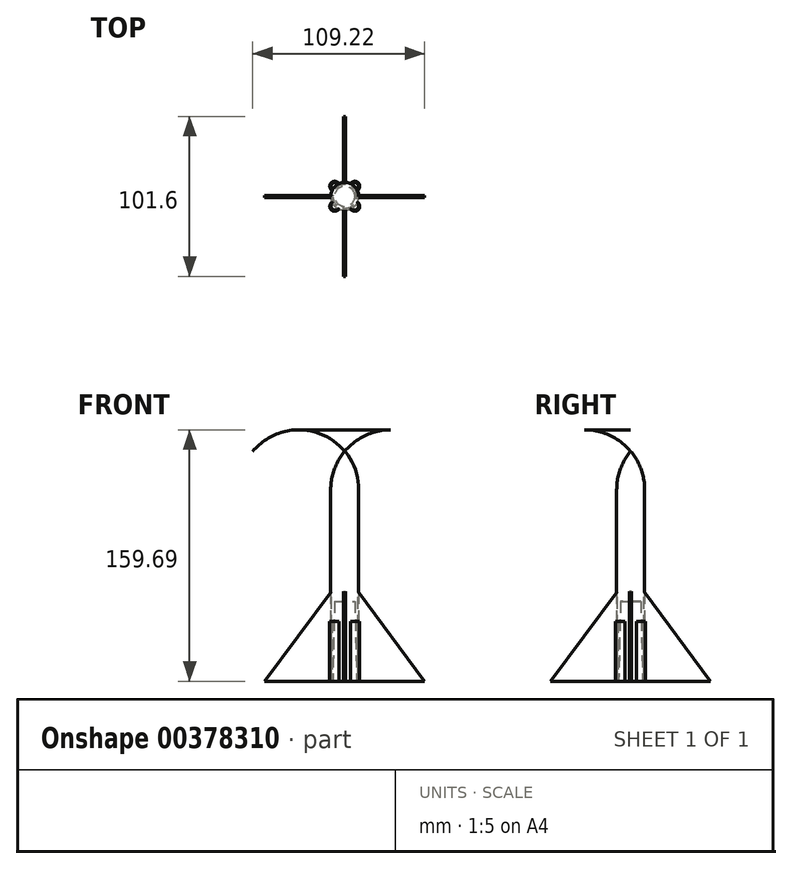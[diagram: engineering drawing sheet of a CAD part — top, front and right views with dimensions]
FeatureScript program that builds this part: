
annotation { "Feature Type Name" : "Feature", "Feature Type Description" : "" }
export const myFeature = defineFeature(function(context is Context, id is Id, definition is map)
    precondition{}
    {
        {
            var Q0;
            Q0=qCreatedBy(makeId("Front.planeOp"),FACE);
            var sketch = newSketch(context, id + "F0", { "sketchPlane" : qUnion([Q0])});
            skLineSegment(sketch, "E0", {"start": v(8.89, 0) * mm, "end": v(8.89, 121.59) * mm});
            skArc(sketch, "E1", {"start": v(8.89, 121.59) * mm, "mid": v(6.6, 134.6) * mm, "end": v(0, 146.05) * mm});
            skLineSegment(sketch, "E2", {"start": v(8.89, 0) * mm, "end": v(7.62, 0) * mm});
            skLineSegment(sketch, "E3", {"start": v(0, 146.05) * mm, "end": v(0, 50.8) * mm});
            skLineSegment(sketch, "E4", {"start": v(0, 50.8) * mm, "end": v(6.48, 50.8) * mm});
            skLineSegment(sketch, "E5", {"start": v(6.48, 50.8) * mm, "end": v(7.62, 0) * mm});
            skSolve(sketch);
        }
        {
            var Q0;
            Q0=qCreatedBy(makeId("Front.planeOp"),FACE);
            var sketch = newSketch(context, id + "F1", { "sketchPlane" : qUnion([Q0])});
            skLineSegment(sketch, "E6", {"start": v(0, 0) * mm, "end": v(0, 146.05) * mm, "construction": true});
            skSolve(sketch);
        }
        {
            var Q0;
            Q0 = qSketchRegion(id + "F0", true);
            var Q1;
            Q1=sQuery(id+"F1.wireOp",EDGE,"E6");
            revolve(context, id + "F2", {"entities" : qUnion([Q0]), "axis" : qUnion([Q1]), "revolveType" : RevolveType.FULL});
        }
        {
            var Q0;
            Q0=qCreatedBy(makeId("Front.planeOp"),FACE);
            var sketch = newSketch(context, id + "F3", { "sketchPlane" : qUnion([Q0])});
            skLineSegment(sketch, "E7", {"start": v(8.38, 0) * mm, "end": v(8.38, 57.15) * mm});
            skLineSegment(sketch, "E8", {"start": v(50.8, 0) * mm, "end": v(8.38, 0) * mm});
            skLineSegment(sketch, "E9", {"start": v(50.8, 0) * mm, "end": v(8.38, 57.15) * mm});
            skSolve(sketch);
        }
        {
            var Q0;
            Q0=makeQuery(id+"F3.imprint","IMPRINT",FACE,{"disambiguationData":[TD([[makeQuery(id+"F3.imprint","IMPRINT",EDGE,{"derivedFrom":sQuery(id+"F3.wireOp",EDGE,"E7")}),-1.0]])]});
            extrude(context, id + "F4", {"entities" : qUnion([Q0]), "endBound" : BoundingType.SYMMETRIC, "oppositeDirection" : true, "depth" : 1.27 * mm});
        }
        {
            var Q0;
            Q0=makeQuery(id+"F4.opExtrude","SWEPT_BODY",BODY,{"disambiguationData":[OSD([sQuery(id+"F3.wireOp",EDGE,"E7"),sQuery(id+"F3.wireOp",EDGE,"E8"),sQuery(id+"F3.wireOp",EDGE,"AmAJtCWf-JhnC-Zdbh-OpwC-5Ge9B8AHfaNN"),sQuery(id+"F3.wireOp",EDGE,"CZrF4tDa-VywW-QGTz-fQES-1TtyQ9VBaDYf"),sQuery(id+"F3.wireOp",EDGE,"y0zfwKda-kGy6-blsG-hRF5-Mtb7aMOzeKxd"),sQuery(id+"F3.wireOp",EDGE,"E9")])]});
            var Q1;
            Q1=makeQuery(id+"F2.opRevolve","SWEPT_FACE",FACE,{"disambiguationData":[OSD([sQuery(id+"F0.wireOp",EDGE,"E0")])]});
            circularPattern(context, id + "F5", {"entities" : qUnion([Q0]), "axis" : qUnion([Q1]), "angle" : 360 * degree, "instanceCount" : 4, "oppositeDirection" : true, "equalSpace" : true});
        }
        {
            var Q0;
            Q0=qCreatedBy(makeId("Top.planeOp"),FACE);
            var sketch = newSketch(context, id + "F6", { "sketchPlane" : qUnion([Q0])});
            skPoint(sketch, "E10.center", {"position": v(0, 0) * mm});
            skArc(sketch, "E11", {"start": v(-8.09, 3.7) * mm, "mid": v(-8.6, 8.6) * mm, "end": v(-3.7, 8.09) * mm});
            skArc(sketch, "E12.1.0", {"start": v(-3.7, -8.09) * mm, "mid": v(-8.6, -8.6) * mm, "end": v(-8.09, -3.7) * mm});
            skArc(sketch, "E12.2.0", {"start": v(8.09, -3.7) * mm, "mid": v(8.6, -8.6) * mm, "end": v(3.7, -8.09) * mm});
            skArc(sketch, "E12.3.0", {"start": v(3.7, 8.09) * mm, "mid": v(8.6, 8.6) * mm, "end": v(8.09, 3.7) * mm});
            skArc(sketch, "E13", {"start": v(-7.98, -3.92) * mm, "mid": v(-7.98, -7.98) * mm, "end": v(-3.92, -7.98) * mm});
            skArc(sketch, "E14.1.0", {"start": v(3.92, -7.98) * mm, "mid": v(7.98, -7.98) * mm, "end": v(7.98, -3.92) * mm});
            skArc(sketch, "E14.2.0", {"start": v(7.98, 3.92) * mm, "mid": v(7.98, 7.98) * mm, "end": v(3.92, 7.98) * mm});
            skArc(sketch, "E14.3.0", {"start": v(-3.92, 7.98) * mm, "mid": v(-7.98, 7.98) * mm, "end": v(-7.98, 3.92) * mm});
            skLineSegment(sketch, "E15", {"start": v(-8.09, -3.7) * mm, "end": v(-7.98, -3.92) * mm});
            skLineSegment(sketch, "E16", {"start": v(-3.92, -7.98) * mm, "end": v(-3.7, -8.09) * mm});
            skLineSegment(sketch, "E17.1.0", {"start": v(7.98, -3.92) * mm, "end": v(8.09, -3.7) * mm});
            skLineSegment(sketch, "E17.1.1", {"start": v(3.7, -8.09) * mm, "end": v(3.92, -7.98) * mm});
            skLineSegment(sketch, "E17.2.0", {"start": v(3.92, 7.98) * mm, "end": v(3.7, 8.09) * mm});
            skLineSegment(sketch, "E17.2.1", {"start": v(8.09, 3.7) * mm, "end": v(7.98, 3.92) * mm});
            skLineSegment(sketch, "E17.3.0", {"start": v(-7.98, 3.92) * mm, "end": v(-8.09, 3.7) * mm});
            skLineSegment(sketch, "E17.3.1", {"start": v(-3.7, 8.09) * mm, "end": v(-3.92, 7.98) * mm});
            skSolve(sketch);
        }
        {
            var Q0;
            Q0 = qSketchRegion(id + "F6", true);
            extrude(context, id + "F7", {"entities" : qUnion([Q0]), "operationType" : NewBodyOperationType.ADD, "depth" : 38.1 * mm});
        }
    });
